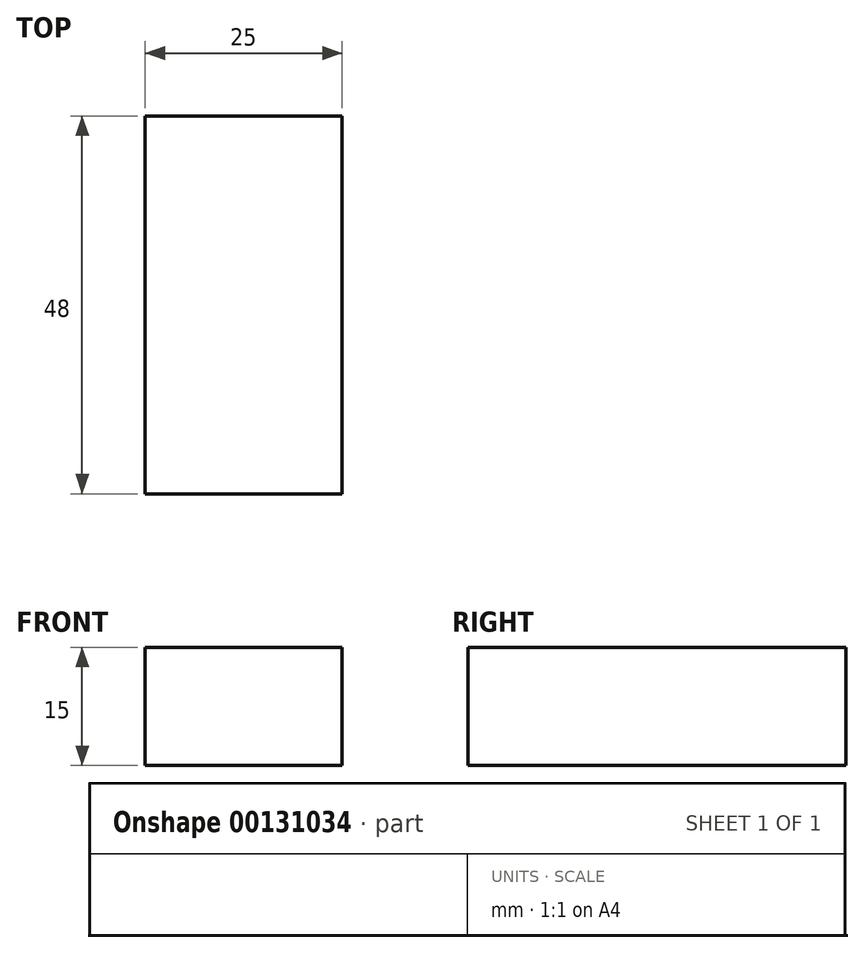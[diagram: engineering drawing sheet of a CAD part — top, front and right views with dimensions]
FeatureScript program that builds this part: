
annotation { "Feature Type Name" : "Feature", "Feature Type Description" : "" }
export const myFeature = defineFeature(function(context is Context, id is Id, definition is map)
    precondition{}
    {
        {
            var Q0;
            Q0=qCreatedBy(makeId("Top.planeOp"),FACE);
            var sketch = newSketch(context, id + "F0", { "sketchPlane" : qUnion([Q0])});
            skLineSegment(sketch, "E0", {"start": v(0, 11.6) * mm, "end": v(1.23, 11.6) * mm});
            skLineSegment(sketch, "E1", {"start": v(1.23, 11.6) * mm, "end": v(1.23, 0) * mm});
            skLineSegment(sketch, "E2.bottom", {"start": v(1.23, 11.6) * mm, "end": v(-23.77, 11.6) * mm});
            skLineSegment(sketch, "E2.top", {"start": v(1.23, -36.4) * mm, "end": v(-23.77, -36.4) * mm});
            skLineSegment(sketch, "E2.left", {"start": v(1.23, 11.6) * mm, "end": v(1.23, -36.4) * mm});
            skLineSegment(sketch, "E2.right", {"start": v(-23.77, 11.6) * mm, "end": v(-23.77, -36.4) * mm});
            skSolve(sketch);
        }
        {
            var Q0;
            {var subQ4=sQuery(id+"F0.wireOp",EDGE,"E2.top");Q0=makeQuery(id+"F0.imprint","IMPRINT",FACE,{"disambiguationData":[TD([[makeQuery(id+"F0.imprint","IMPRINT",EDGE,{"derivedFrom":subQ4}),-1.0]])]});}
            extrude(context, id + "F1", {"entities" : qUnion([Q0]), "depth" : 15 * mm});
        }
    });
